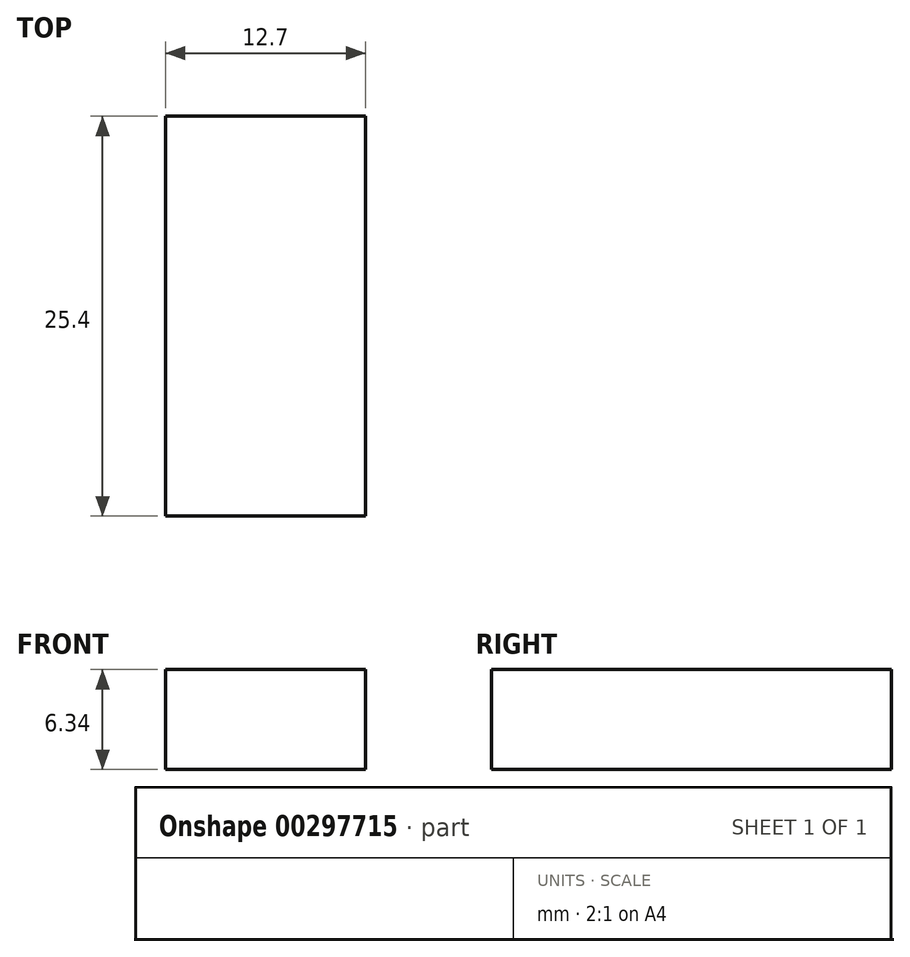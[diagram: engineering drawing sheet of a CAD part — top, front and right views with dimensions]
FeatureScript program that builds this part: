
annotation { "Feature Type Name" : "Feature", "Feature Type Description" : "" }
export const myFeature = defineFeature(function(context is Context, id is Id, definition is map)
    precondition{}
    {
        {
            var Q0;
            Q0=qCreatedBy(makeId("Front.planeOp"),FACE);
            var sketch = newSketch(context, id + "F0", { "sketchPlane" : qUnion([Q0])});
            skLineSegment(sketch, "E0.bottom", {"start": v(6.35, 3.18) * mm, "end": v(-6.35, 3.18) * mm});
            skLineSegment(sketch, "E0.top", {"start": v(6.35, -3.18) * mm, "end": v(-6.35, -3.18) * mm});
            skLineSegment(sketch, "E0.left", {"start": v(6.35, 3.18) * mm, "end": v(6.35, -3.18) * mm});
            skLineSegment(sketch, "E0.right", {"start": v(-6.35, 3.18) * mm, "end": v(-6.35, -3.18) * mm});
            skPoint(sketch, "E0.middle", {"position": v(0, 0) * mm});
            skSolve(sketch);
        }
        {
            var Q0;
            Q0 = qSketchRegion(id + "F0", true);
            extrude(context, id + "F1", {"entities" : qUnion([Q0]), "depth" : 25.4 * mm});
        }
    });
